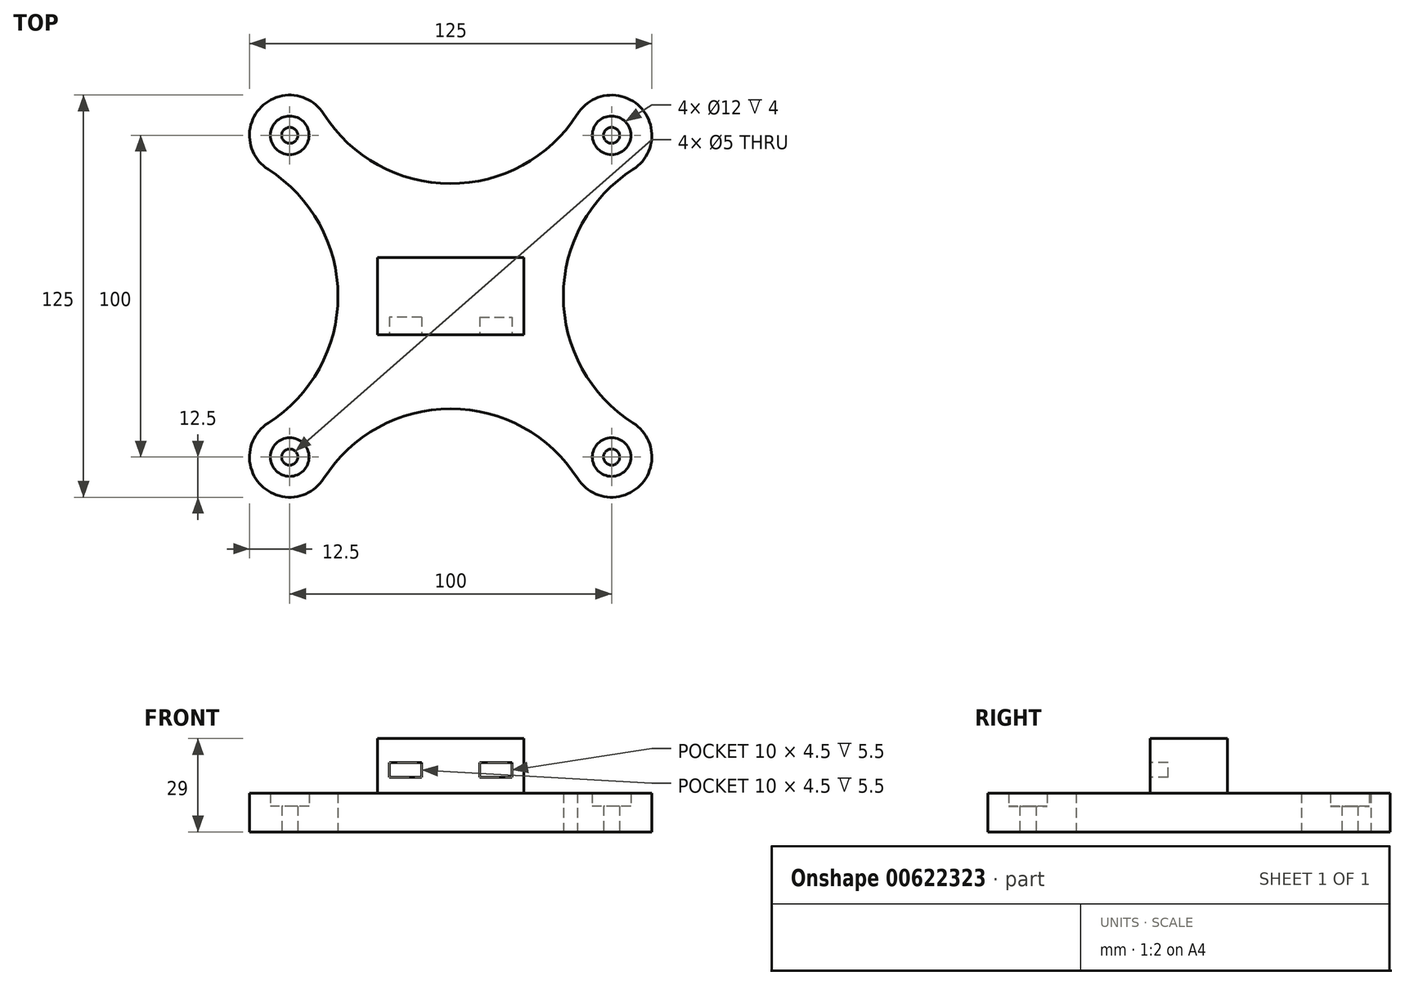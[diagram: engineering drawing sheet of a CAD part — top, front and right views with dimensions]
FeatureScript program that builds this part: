
annotation { "Feature Type Name" : "Feature", "Feature Type Description" : "" }
export const myFeature = defineFeature(function(context is Context, id is Id, definition is map)
    precondition{}
    {
        {
            var Q0;
            Q0=qCreatedBy(makeId("Top.planeOp"),FACE);
            var sketch = newSketch(context, id + "F0", { "sketchPlane" : qUnion([Q0])});
            skLineSegment(sketch, "E0.bottom", {"start": v(50, -50) * mm, "end": v(-50, -50) * mm});
            skLineSegment(sketch, "E0.top", {"start": v(50, 50) * mm, "end": v(-50, 50) * mm});
            skLineSegment(sketch, "E0.left", {"start": v(50, -50) * mm, "end": v(50, 50) * mm});
            skLineSegment(sketch, "E0.right", {"start": v(-50, -50) * mm, "end": v(-50, 50) * mm});
            skPoint(sketch, "E0.middle", {"position": v(0, 0) * mm});
            skCircle(sketch, "E1", {"center": v(50, 50) * mm, "radius": 2.5 * mm});
            skCircle(sketch, "E2", {"center": v(50, -50) * mm, "radius": 2.5 * mm});
            skCircle(sketch, "E3", {"center": v(-50, -50) * mm, "radius": 2.5 * mm});
            skCircle(sketch, "E4", {"center": v(-50, 50) * mm, "radius": 2.5 * mm});
            skCircle(sketch, "E5", {"center": v(50, 50) * mm, "radius": 6 * mm});
            skCircle(sketch, "E6", {"center": v(50, -50) * mm, "radius": 6 * mm});
            skCircle(sketch, "E7", {"center": v(-50, -50) * mm, "radius": 6 * mm});
            skCircle(sketch, "E8", {"center": v(-50, 50) * mm, "radius": 6 * mm});
            skCircle(sketch, "E9", {"center": v(50, 50) * mm, "radius": 12.5 * mm});
            skCircle(sketch, "E10", {"center": v(50, -50) * mm, "radius": 12.5 * mm});
            skCircle(sketch, "E11", {"center": v(-50, -50) * mm, "radius": 12.5 * mm});
            skCircle(sketch, "E12", {"center": v(-50, 50) * mm, "radius": 12.5 * mm});
            skLineSegment(sketch, "E13.bottom", {"start": v(22.75, -12) * mm, "end": v(-22.75, -12) * mm});
            skLineSegment(sketch, "E13.top", {"start": v(22.75, 12) * mm, "end": v(-22.75, 12) * mm});
            skLineSegment(sketch, "E13.left", {"start": v(22.75, -12) * mm, "end": v(22.75, 12) * mm});
            skLineSegment(sketch, "E13.right", {"start": v(-22.75, -12) * mm, "end": v(-22.75, 12) * mm});
            skLineSegment(sketch, "E14", {"start": v(0, 0) * mm, "end": v(-35, 0) * mm});
            skPoint(sketch, "E14.endSnap0", {"position": v(-22.75, 0) * mm});
            skLineSegment(sketch, "E15", {"start": v(0, 0) * mm, "end": v(35, 0) * mm});
            skPoint(sketch, "E15.endSnap0", {"position": v(22.75, 0) * mm});
            skLineSegment(sketch, "E16", {"start": v(0, 0) * mm, "end": v(0, 35) * mm});
            skLineSegment(sketch, "E17", {"start": v(0, 0) * mm, "end": v(0, -35) * mm});
            skPoint(sketch, "E17.endSnap0", {"position": v(0, -12) * mm});
            skArc(sketch, "E18", {"start": v(-39.44, 56.7) * mm, "mid": v(-0.14, 35) * mm, "end": v(39.3, 56.46) * mm});
            skArc(sketch, "E19", {"start": v(58.89, 40.75) * mm, "mid": v(35, 0.24) * mm, "end": v(58.48, -40.52) * mm});
            skArc(sketch, "E20", {"start": v(42.84, -63.1) * mm, "mid": v(0.33, -35) * mm, "end": v(-42.57, -62.49) * mm});
            skArc(sketch, "E21", {"start": v(-63.5, -43.01) * mm, "mid": v(-35, -0.76) * mm, "end": v(-62.11, 42.4) * mm});
            skLineSegment(sketch, "E22", {"start": v(39.3, 56.46) * mm, "end": v(39.37, 56.57) * mm});
            skSolve(sketch);
        }
        {
            var Q0;
            {var subQ0=sQuery(id+"F0.wireOp",EDGE,"E20");var subQ1=sQuery(id+"F0.wireOp",EDGE,"E0.bottom");var subQ2=makeQuery(id+"F0.imprint","INTERSECT",VERTEX,{"disambiguationData":[OD(0.0)],"derivedFrom":[subQ1,subQ0]});Q0=makeQuery(id+"F0.imprint","IMPRINT",FACE,{"disambiguationData":[TD([[makeQuery(id+"F0.imprint","IMPRINT",EDGE,{"disambiguationData":[TD([[subQ2,1.0]])],"derivedFrom":subQ1}),1.0]])]});}
            var Q1;
            {var subQ0=sQuery(id+"F0.wireOp",EDGE,"E20");var subQ1=sQuery(id+"F0.wireOp",EDGE,"E0.bottom");var subQ2=makeQuery(id+"F0.imprint","INTERSECT",VERTEX,{"disambiguationData":[OD(1.0)],"derivedFrom":[subQ1,subQ0]});Q1=makeQuery(id+"F0.imprint","IMPRINT",FACE,{"disambiguationData":[TD([[makeQuery(id+"F0.imprint","IMPRINT",EDGE,{"disambiguationData":[TD([[subQ2,-1.0]])],"derivedFrom":subQ1}),1.0]])]});}
            var Q2;
            {var subQ0=sQuery(id+"F0.wireOp",EDGE,"E18");var subQ1=sQuery(id+"F0.wireOp",EDGE,"E0.top");var subQ2=makeQuery(id+"F0.imprint","INTERSECT",VERTEX,{"disambiguationData":[OD(1.0)],"derivedFrom":[subQ1,subQ0]});Q2=makeQuery(id+"F0.imprint","IMPRINT",FACE,{"disambiguationData":[TD([[makeQuery(id+"F0.imprint","IMPRINT",EDGE,{"disambiguationData":[TD([[subQ2,-1.0]])],"derivedFrom":subQ1}),-1.0]])]});}
            var Q3;
            {var subQ0=sQuery(id+"F0.wireOp",EDGE,"E19");var subQ1=sQuery(id+"F0.wireOp",EDGE,"E0.left");var subQ2=makeQuery(id+"F0.imprint","INTERSECT",VERTEX,{"disambiguationData":[OD(0.0)],"derivedFrom":[subQ1,subQ0]});Q3=makeQuery(id+"F0.imprint","IMPRINT",FACE,{"disambiguationData":[TD([[makeQuery(id+"F0.imprint","IMPRINT",EDGE,{"disambiguationData":[TD([[subQ2,1.0]])],"derivedFrom":subQ1}),-1.0]])]});}
            var Q4;
            {var subQ0=sQuery(id+"F0.wireOp",EDGE,"E19");var subQ1=sQuery(id+"F0.wireOp",EDGE,"E0.left");var subQ2=makeQuery(id+"F0.imprint","INTERSECT",VERTEX,{"disambiguationData":[OD(1.0)],"derivedFrom":[subQ1,subQ0]});Q4=makeQuery(id+"F0.imprint","IMPRINT",FACE,{"disambiguationData":[TD([[makeQuery(id+"F0.imprint","IMPRINT",EDGE,{"disambiguationData":[TD([[subQ2,-1.0]])],"derivedFrom":subQ1}),-1.0]])]});}
            var Q5;
            {var subQ0=sQuery(id+"F0.wireOp",EDGE,"E21");var subQ1=sQuery(id+"F0.wireOp",EDGE,"E0.right");var subQ2=makeQuery(id+"F0.imprint","INTERSECT",VERTEX,{"disambiguationData":[OD(0.0)],"derivedFrom":[subQ1,subQ0]});Q5=makeQuery(id+"F0.imprint","IMPRINT",FACE,{"disambiguationData":[TD([[makeQuery(id+"F0.imprint","IMPRINT",EDGE,{"disambiguationData":[TD([[subQ2,1.0]])],"derivedFrom":subQ1}),1.0]])]});}
            var Q6;
            {var subQ0=sQuery(id+"F0.wireOp",EDGE,"E21");var subQ1=sQuery(id+"F0.wireOp",EDGE,"E0.right");var subQ2=makeQuery(id+"F0.imprint","INTERSECT",VERTEX,{"disambiguationData":[OD(1.0)],"derivedFrom":[subQ1,subQ0]});Q6=makeQuery(id+"F0.imprint","IMPRINT",FACE,{"disambiguationData":[TD([[makeQuery(id+"F0.imprint","IMPRINT",EDGE,{"disambiguationData":[TD([[subQ2,-1.0]])],"derivedFrom":subQ1}),1.0]])]});}
            var Q7;
            {var subQ0=sQuery(id+"F0.wireOp",EDGE,"E9");var subQ1=sQuery(id+"F0.wireOp",EDGE,"E0.top");var subQ2=makeQuery(id+"F0.imprint","INTERSECT",VERTEX,{"derivedFrom":[subQ1,subQ0]});Q7=makeQuery(id+"F0.imprint","IMPRINT",FACE,{"disambiguationData":[TD([[makeQuery(id+"F0.imprint","IMPRINT",EDGE,{"disambiguationData":[TD([[subQ2,1.0]])],"derivedFrom":subQ1}),1.0]])]});}
            var Q8;
            {var subQ0=sQuery(id+"F0.wireOp",EDGE,"E9");var subQ5=sQuery(id+"F0.wireOp",EDGE,"E0.top");var subQ8=makeQuery(id+"F0.imprint","INTERSECT",VERTEX,{"derivedFrom":[subQ5,subQ0]});Q8=makeQuery(id+"F0.imprint","IMPRINT",FACE,{"disambiguationData":[TD([[makeQuery(id+"F0.imprint","IMPRINT",EDGE,{"disambiguationData":[TD([[subQ8,1.0]])],"derivedFrom":subQ5}),-1.0]])]});}
            var Q9;
            {var subQ4=sQuery(id+"F0.wireOp",EDGE,"E6");var subQ6=sQuery(id+"F0.wireOp",EDGE,"E0.bottom");var subQ7=makeQuery(id+"F0.imprint","INTERSECT",VERTEX,{"derivedFrom":[subQ6,subQ4]});Q9=makeQuery(id+"F0.imprint","IMPRINT",FACE,{"disambiguationData":[TD([[makeQuery(id+"F0.imprint","IMPRINT",EDGE,{"disambiguationData":[TD([[subQ7,-1.0]])],"derivedFrom":subQ6}),1.0]])]});}
            var Q10;
            {var subQ0=sQuery(id+"F0.wireOp",EDGE,"E11");var subQ5=sQuery(id+"F0.wireOp",EDGE,"E0.bottom");var subQ9=makeQuery(id+"F0.imprint","INTERSECT",VERTEX,{"derivedFrom":[subQ5,subQ0]});Q10=makeQuery(id+"F0.imprint","IMPRINT",FACE,{"disambiguationData":[TD([[makeQuery(id+"F0.imprint","IMPRINT",EDGE,{"disambiguationData":[TD([[subQ9,-1.0]])],"derivedFrom":subQ5}),1.0]])]});}
            var Q11;
            {var subQ0=sQuery(id+"F0.wireOp",EDGE,"E12");var subQ2=sQuery(id+"F0.wireOp",EDGE,"E0.top");var subQ3=makeQuery(id+"F0.imprint","INTERSECT",VERTEX,{"derivedFrom":[subQ2,subQ0]});Q11=makeQuery(id+"F0.imprint","IMPRINT",FACE,{"disambiguationData":[TD([[makeQuery(id+"F0.imprint","IMPRINT",EDGE,{"disambiguationData":[TD([[subQ3,-1.0]])],"derivedFrom":subQ2}),-1.0]])]});}
            var Q12;
            {var subQ5=sQuery(id+"F0.wireOp",EDGE,"E18");var subQ12=sQuery(id+"F0.wireOp",EDGE,"E0.top");var subQ13=makeQuery(id+"F0.imprint","INTERSECT",VERTEX,{"disambiguationData":[OD(0.0)],"derivedFrom":[subQ12,subQ5]});Q12=makeQuery(id+"F0.imprint","IMPRINT",FACE,{"disambiguationData":[TD([[makeQuery(id+"F0.imprint","IMPRINT",EDGE,{"disambiguationData":[TD([[subQ13,1.0]])],"derivedFrom":subQ12}),1.0]])]});}
            var Q13;
            {var subQ6=sQuery(id+"F0.wireOp",EDGE,"E0.bottom");var subQ15=sQuery(id+"F0.wireOp",EDGE,"E20");var subQ16=makeQuery(id+"F0.imprint","INTERSECT",VERTEX,{"disambiguationData":[OD(0.0)],"derivedFrom":[subQ6,subQ15]});Q13=makeQuery(id+"F0.imprint","IMPRINT",FACE,{"disambiguationData":[TD([[makeQuery(id+"F0.imprint","IMPRINT",EDGE,{"disambiguationData":[TD([[subQ16,1.0]])],"derivedFrom":subQ6}),-1.0]])]});}
            var Q14;
            {var subQ6=sQuery(id+"F0.wireOp",EDGE,"E0.bottom");var subQ10=sQuery(id+"F0.wireOp",EDGE,"E20");var subQ12=makeQuery(id+"F0.imprint","INTERSECT",VERTEX,{"disambiguationData":[OD(1.0)],"derivedFrom":[subQ6,subQ10]});Q14=makeQuery(id+"F0.imprint","IMPRINT",FACE,{"disambiguationData":[TD([[makeQuery(id+"F0.imprint","IMPRINT",EDGE,{"disambiguationData":[TD([[subQ12,-1.0]])],"derivedFrom":subQ6}),-1.0]])]});}
            var Q15;
            {var subQ6=sQuery(id+"F0.wireOp",EDGE,"E0.top");var subQ15=sQuery(id+"F0.wireOp",EDGE,"E18");var subQ16=makeQuery(id+"F0.imprint","INTERSECT",VERTEX,{"disambiguationData":[OD(1.0)],"derivedFrom":[subQ6,subQ15]});Q15=makeQuery(id+"F0.imprint","IMPRINT",FACE,{"disambiguationData":[TD([[makeQuery(id+"F0.imprint","IMPRINT",EDGE,{"disambiguationData":[TD([[subQ16,-1.0]])],"derivedFrom":subQ6}),1.0]])]});}
            var Q16;
            {var subQ0=sQuery(id+"F0.wireOp",EDGE,"E11");var subQ1=sQuery(id+"F0.wireOp",EDGE,"E0.bottom");var subQ2=makeQuery(id+"F0.imprint","INTERSECT",VERTEX,{"derivedFrom":[subQ1,subQ0]});Q16=makeQuery(id+"F0.imprint","IMPRINT",FACE,{"disambiguationData":[TD([[makeQuery(id+"F0.imprint","IMPRINT",EDGE,{"disambiguationData":[TD([[subQ2,-1.0]])],"derivedFrom":subQ1}),-1.0]])]});}
            var Q17;
            {var subQ0=sQuery(id+"F0.wireOp",EDGE,"E12");var subQ1=sQuery(id+"F0.wireOp",EDGE,"E0.top");var subQ2=makeQuery(id+"F0.imprint","INTERSECT",VERTEX,{"derivedFrom":[subQ1,subQ0]});Q17=makeQuery(id+"F0.imprint","IMPRINT",FACE,{"disambiguationData":[TD([[makeQuery(id+"F0.imprint","IMPRINT",EDGE,{"disambiguationData":[TD([[subQ2,-1.0]])],"derivedFrom":subQ1}),1.0]])]});}
            var Q18;
            {var subQ0=sQuery(id+"F0.wireOp",EDGE,"E6");var subQ1=sQuery(id+"F0.wireOp",EDGE,"E0.bottom");var subQ2=makeQuery(id+"F0.imprint","INTERSECT",VERTEX,{"derivedFrom":[subQ1,subQ0]});Q18=makeQuery(id+"F0.imprint","IMPRINT",FACE,{"disambiguationData":[TD([[makeQuery(id+"F0.imprint","IMPRINT",EDGE,{"disambiguationData":[TD([[subQ2,-1.0]])],"derivedFrom":subQ1}),-1.0]])]});}
            var Q19;
            {var subQ5=sQuery(id+"F0.wireOp",EDGE,"E22");Q19=makeQuery(id+"F0.imprint","IMPRINT",FACE,{"disambiguationData":[TD([[makeQuery(id+"F0.imprint","IMPRINT",EDGE,{"derivedFrom":subQ5}),-1.0]])]});}
            extrude(context, id + "F1", {"entities" : qUnion([Q0, Q1, Q2, Q3, Q4, Q5, Q6, Q7, Q8, Q9, Q10, Q11, Q12, Q13, Q14, Q15, Q16, Q17, Q18, Q19]), "depth" : 12 * mm, "offsetDistance" : 25 * mm});
        }
        {
            var Q0;
            {var subQ0=sQuery(id+"F0.wireOp",EDGE,"E13.right");var subQ1=sQuery(id+"F0.wireOp",EDGE,"E13.top");var subQ2=makeQuery(id+"F0.imprint","INTERSECT",VERTEX,{"derivedFrom":[subQ1,subQ0]});Q0=makeQuery(id+"F0.imprint","IMPRINT",FACE,{"disambiguationData":[TD([[makeQuery(id+"F0.imprint","IMPRINT",EDGE,{"disambiguationData":[TD([[subQ2,1.0]])],"derivedFrom":subQ1}),1.0]])]});}
            var Q1;
            {var subQ0=sQuery(id+"F0.wireOp",EDGE,"E13.left");var subQ1=sQuery(id+"F0.wireOp",EDGE,"E13.top");var subQ2=makeQuery(id+"F0.imprint","INTERSECT",VERTEX,{"derivedFrom":[subQ1,subQ0]});Q1=makeQuery(id+"F0.imprint","IMPRINT",FACE,{"disambiguationData":[TD([[makeQuery(id+"F0.imprint","IMPRINT",EDGE,{"disambiguationData":[TD([[subQ2,-1.0]])],"derivedFrom":subQ1}),1.0]])]});}
            var Q2;
            {var subQ0=sQuery(id+"F0.wireOp",EDGE,"E13.left");var subQ1=sQuery(id+"F0.wireOp",EDGE,"E13.bottom");var subQ2=makeQuery(id+"F0.imprint","INTERSECT",VERTEX,{"derivedFrom":[subQ1,subQ0]});Q2=makeQuery(id+"F0.imprint","IMPRINT",FACE,{"disambiguationData":[TD([[makeQuery(id+"F0.imprint","IMPRINT",EDGE,{"disambiguationData":[TD([[subQ2,-1.0]])],"derivedFrom":subQ1}),-1.0]])]});}
            var Q3;
            {var subQ0=sQuery(id+"F0.wireOp",EDGE,"E13.right");var subQ1=sQuery(id+"F0.wireOp",EDGE,"E13.bottom");var subQ2=makeQuery(id+"F0.imprint","INTERSECT",VERTEX,{"derivedFrom":[subQ1,subQ0]});Q3=makeQuery(id+"F0.imprint","IMPRINT",FACE,{"disambiguationData":[TD([[makeQuery(id+"F0.imprint","IMPRINT",EDGE,{"disambiguationData":[TD([[subQ2,1.0]])],"derivedFrom":subQ1}),-1.0]])]});}
            extrude(context, id + "F2", {"entities" : qUnion([Q0, Q1, Q2, Q3]), "operationType" : NewBodyOperationType.ADD, "depth" : 29 * mm, "offsetDistance" : 25 * mm});
        }
        {
            var Q0;
            {var subQ0=sQuery(id+"F0.wireOp",EDGE,"E8");var subQ1=sQuery(id+"F0.wireOp",EDGE,"E0.top");var subQ2=makeQuery(id+"F0.imprint","INTERSECT",VERTEX,{"derivedFrom":[subQ1,subQ0]});Q0=makeQuery(id+"F0.imprint","IMPRINT",FACE,{"disambiguationData":[TD([[makeQuery(id+"F0.imprint","IMPRINT",EDGE,{"disambiguationData":[TD([[subQ2,-1.0]])],"derivedFrom":subQ1}),-1.0]])]});}
            var Q1;
            {var subQ0=sQuery(id+"F0.wireOp",EDGE,"E8");var subQ1=sQuery(id+"F0.wireOp",EDGE,"E0.top");var subQ2=makeQuery(id+"F0.imprint","INTERSECT",VERTEX,{"derivedFrom":[subQ1,subQ0]});Q1=makeQuery(id+"F0.imprint","IMPRINT",FACE,{"disambiguationData":[TD([[makeQuery(id+"F0.imprint","IMPRINT",EDGE,{"disambiguationData":[TD([[subQ2,-1.0]])],"derivedFrom":subQ1}),1.0]])]});}
            var Q2;
            {var subQ0=sQuery(id+"F0.wireOp",EDGE,"E1");var subQ1=sQuery(id+"F0.wireOp",EDGE,"E0.top");var subQ2=makeQuery(id+"F0.imprint","INTERSECT",VERTEX,{"derivedFrom":[subQ1,subQ0]});Q2=makeQuery(id+"F0.imprint","IMPRINT",FACE,{"disambiguationData":[TD([[makeQuery(id+"F0.imprint","IMPRINT",EDGE,{"disambiguationData":[TD([[subQ2,-1.0]])],"derivedFrom":subQ1}),-1.0]])]});}
            var Q3;
            {var subQ0=sQuery(id+"F0.wireOp",EDGE,"E1");var subQ1=sQuery(id+"F0.wireOp",EDGE,"E0.top");var subQ2=makeQuery(id+"F0.imprint","INTERSECT",VERTEX,{"derivedFrom":[subQ1,subQ0]});Q3=makeQuery(id+"F0.imprint","IMPRINT",FACE,{"disambiguationData":[TD([[makeQuery(id+"F0.imprint","IMPRINT",EDGE,{"disambiguationData":[TD([[subQ2,-1.0]])],"derivedFrom":subQ1}),1.0]])]});}
            var Q4;
            {var subQ0=sQuery(id+"F0.wireOp",EDGE,"E2");var subQ1=sQuery(id+"F0.wireOp",EDGE,"E0.bottom");var subQ2=makeQuery(id+"F0.imprint","INTERSECT",VERTEX,{"derivedFrom":[subQ1,subQ0]});Q4=makeQuery(id+"F0.imprint","IMPRINT",FACE,{"disambiguationData":[TD([[makeQuery(id+"F0.imprint","IMPRINT",EDGE,{"disambiguationData":[TD([[subQ2,-1.0]])],"derivedFrom":subQ1}),-1.0]])]});}
            var Q5;
            {var subQ0=sQuery(id+"F0.wireOp",EDGE,"E2");var subQ1=sQuery(id+"F0.wireOp",EDGE,"E0.bottom");var subQ2=makeQuery(id+"F0.imprint","INTERSECT",VERTEX,{"derivedFrom":[subQ1,subQ0]});Q5=makeQuery(id+"F0.imprint","IMPRINT",FACE,{"disambiguationData":[TD([[makeQuery(id+"F0.imprint","IMPRINT",EDGE,{"disambiguationData":[TD([[subQ2,-1.0]])],"derivedFrom":subQ1}),1.0]])]});}
            var Q6;
            {var subQ0=sQuery(id+"F0.wireOp",EDGE,"E7");var subQ1=sQuery(id+"F0.wireOp",EDGE,"E0.bottom");var subQ2=makeQuery(id+"F0.imprint","INTERSECT",VERTEX,{"derivedFrom":[subQ1,subQ0]});Q6=makeQuery(id+"F0.imprint","IMPRINT",FACE,{"disambiguationData":[TD([[makeQuery(id+"F0.imprint","IMPRINT",EDGE,{"disambiguationData":[TD([[subQ2,-1.0]])],"derivedFrom":subQ1}),-1.0]])]});}
            var Q7;
            {var subQ0=sQuery(id+"F0.wireOp",EDGE,"E7");var subQ1=sQuery(id+"F0.wireOp",EDGE,"E0.bottom");var subQ2=makeQuery(id+"F0.imprint","INTERSECT",VERTEX,{"derivedFrom":[subQ1,subQ0]});Q7=makeQuery(id+"F0.imprint","IMPRINT",FACE,{"disambiguationData":[TD([[makeQuery(id+"F0.imprint","IMPRINT",EDGE,{"disambiguationData":[TD([[subQ2,-1.0]])],"derivedFrom":subQ1}),1.0]])]});}
            extrude(context, id + "F3", {"entities" : qUnion([Q0, Q1, Q2, Q3, Q4, Q5, Q6, Q7]), "operationType" : NewBodyOperationType.ADD, "depth" : 8 * mm, "offsetDistance" : 25 * mm});
        }
        {
            var Q0;
            Q0=makeQuery(id+"F2.opExtrude","SWEPT_FACE",FACE,{"disambiguationData":[OSD([sQuery(id+"F0.wireOp",EDGE,"E13.bottom")])]});
            var sketch = newSketch(context, id + "F4", { "sketchPlane" : qUnion([Q0])});
            skLineSegment(sketch, "E23", {"start": v(0, 29) * mm, "end": v(0, 21.5) * mm});
            skPoint(sketch, "E23.endSnap0", {"position": v(0, 29) * mm});
            skLineSegment(sketch, "E24", {"start": v(0, 21.5) * mm, "end": v(19, 21.5) * mm});
            skLineSegment(sketch, "E25", {"start": v(0, 21.5) * mm, "end": v(-19, 21.5) * mm});
            skLineSegment(sketch, "E26", {"start": v(-19, 21.5) * mm, "end": v(-19, 17) * mm});
            skLineSegment(sketch, "E27", {"start": v(19, 21.5) * mm, "end": v(19, 17) * mm});
            skLineSegment(sketch, "E28", {"start": v(-19, 17) * mm, "end": v(-9, 17) * mm});
            skLineSegment(sketch, "E29", {"start": v(-9, 17) * mm, "end": v(-9, 21.5) * mm});
            skLineSegment(sketch, "E30", {"start": v(19, 17) * mm, "end": v(9, 17) * mm});
            skLineSegment(sketch, "E31", {"start": v(9, 17) * mm, "end": v(9, 21.5) * mm});
            skSolve(sketch);
        }
        {
            var Q0;
            {var subQ0=sQuery(id+"F4.wireOp",EDGE,"E26");Q0=makeQuery(id+"F4.imprint","IMPRINT",FACE,{"disambiguationData":[TD([[makeQuery(id+"F4.imprint","IMPRINT",EDGE,{"derivedFrom":subQ0}),1.0]])]});}
            var Q1;
            {var subQ0=sQuery(id+"F4.wireOp",EDGE,"E27");Q1=makeQuery(id+"F4.imprint","IMPRINT",FACE,{"disambiguationData":[TD([[makeQuery(id+"F4.imprint","IMPRINT",EDGE,{"derivedFrom":subQ0}),-1.0]])]});}
            extrude(context, id + "F5", {"entities" : qUnion([Q0, Q1]), "operationType" : NewBodyOperationType.REMOVE, "oppositeDirection" : true, "depth" : 5.5 * mm, "offsetDistance" : 25 * mm});
        }
    });
